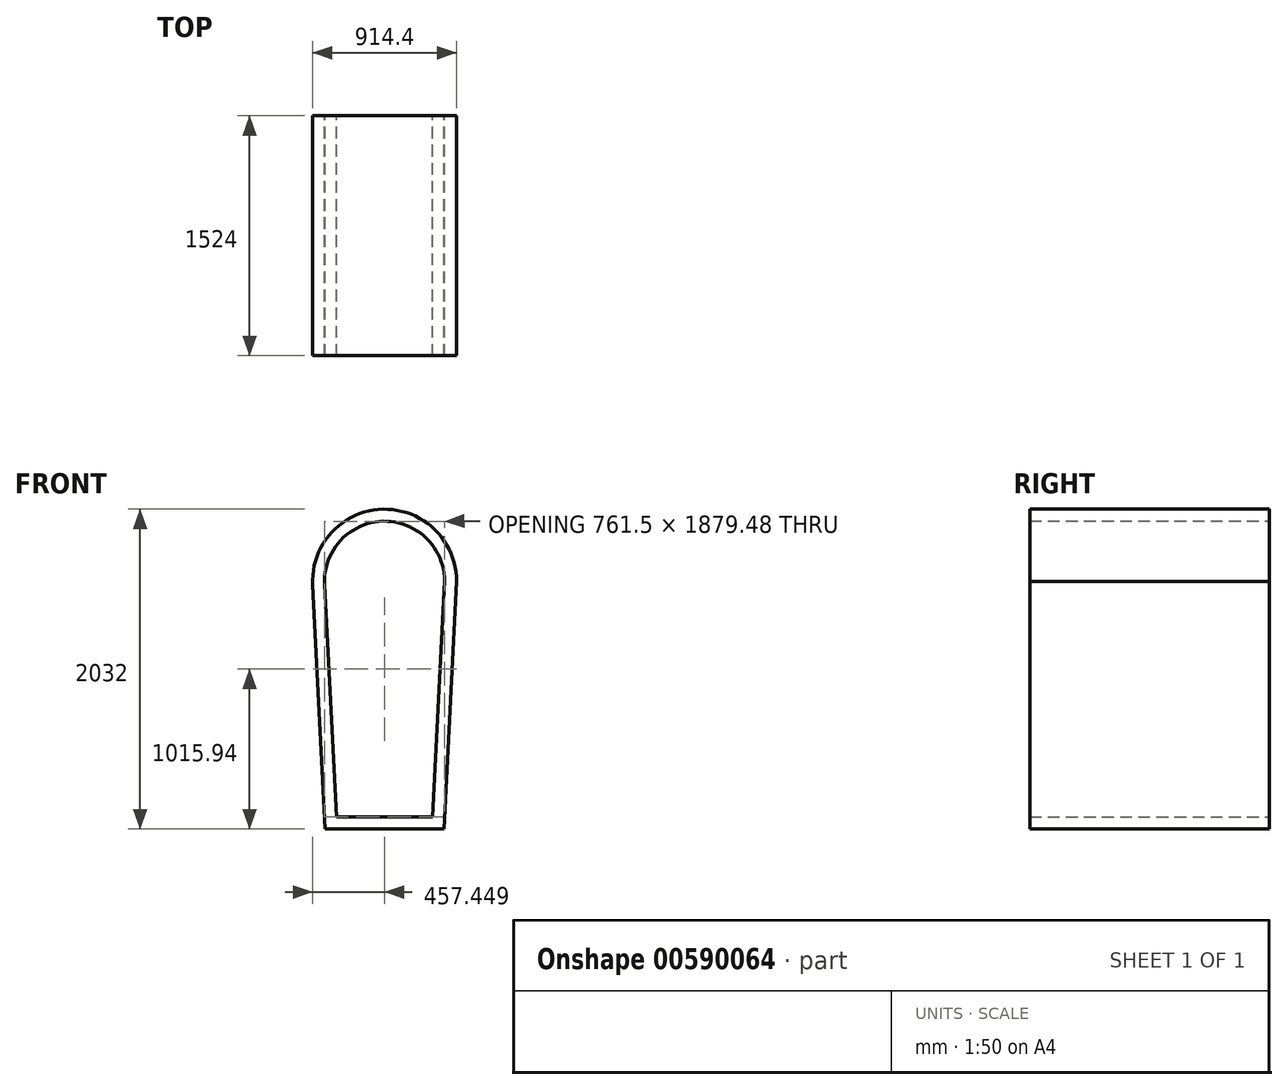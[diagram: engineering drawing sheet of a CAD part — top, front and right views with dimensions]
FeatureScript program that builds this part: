
annotation { "Feature Type Name" : "Feature", "Feature Type Description" : "" }
export const myFeature = defineFeature(function(context is Context, id is Id, definition is map)
    precondition{}
    {
        {
            var Q0;
            Q0=qCreatedBy(makeId("Front.planeOp"),FACE);
            var sketch = newSketch(context, id + "F0", { "sketchPlane" : qUnion([Q0])});
            skLineSegment(sketch, "E0.bottom", {"start": v(381, -939.8) * mm, "end": v(-381, -939.8) * mm, "construction": true});
            skLineSegment(sketch, "E0.top", {"start": v(381, 939.8) * mm, "end": v(-381, 939.8) * mm, "construction": true});
            skLineSegment(sketch, "E0.left", {"start": v(381, -939.8) * mm, "end": v(381, 939.8) * mm, "construction": true});
            skLineSegment(sketch, "E0.right", {"start": v(-381, -939.8) * mm, "end": v(-381, 939.8) * mm, "construction": true});
            skPoint(sketch, "E0.middle", {"position": v(0, 0) * mm});
            skLineSegment(sketch, "E1", {"start": v(0, 939.8) * mm, "end": v(0, -939.8) * mm, "construction": true});
            skArc(sketch, "E2", {"start": v(381, 558.8) * mm, "mid": v(-9.74, 939.68) * mm, "end": v(-380.5, 539.33) * mm});
            skLineSegment(sketch, "E3", {"start": v(-304.8, -939.8) * mm, "end": v(304.8, -939.8) * mm});
            skLineSegment(sketch, "E4", {"start": v(-304.8, -939.8) * mm, "end": v(-380.5, 539.33) * mm});
            skLineSegment(sketch, "E5", {"start": v(304.8, -939.8) * mm, "end": v(381, 558.8) * mm});
            skArc(sketch, "E6.0", {"start": v(457.2, 556.78) * mm, "mid": v(-10.68, 1015.88) * mm, "end": v(-456.6, 535.43) * mm});
            skLineSegment(sketch, "E6.1", {"start": v(377.22, -1016) * mm, "end": v(457.2, 556.78) * mm});
            skLineSegment(sketch, "E6.2", {"start": v(-377.2, -1016) * mm, "end": v(377.22, -1016) * mm});
            skLineSegment(sketch, "E6.3", {"start": v(-377.2, -1016) * mm, "end": v(-456.6, 535.43) * mm});
            skSolve(sketch);
        }
        {
            var Q0;
            Q0=makeQuery(id+"F0.imprint","IMPRINT",FACE,{"disambiguationData":[TD([[makeQuery(id+"F0.imprint","IMPRINT",EDGE,{"derivedFrom":sQuery(id+"F0.wireOp",EDGE,"E2")}),-1.0]])]});
            extrude(context, id + "F1", {"entities" : qUnion([Q0]), "depth" : 1524 * mm, "offsetDistance" : 25.4 * mm});
        }
    });
